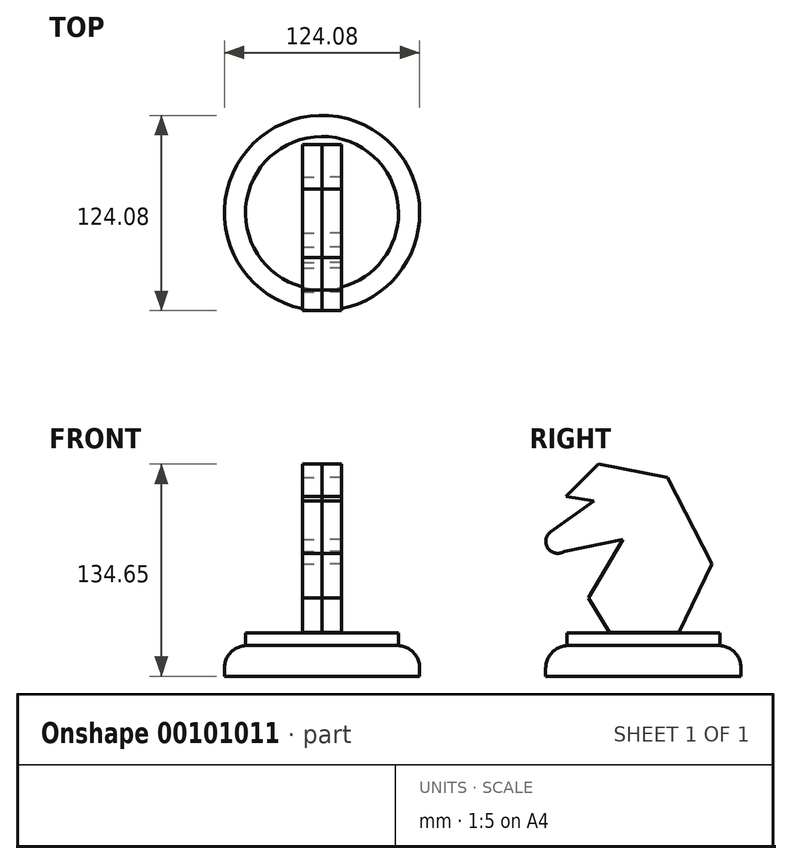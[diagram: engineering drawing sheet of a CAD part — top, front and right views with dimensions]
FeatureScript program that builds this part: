
annotation { "Feature Type Name" : "Feature", "Feature Type Description" : "" }
export const myFeature = defineFeature(function(context is Context, id is Id, definition is map)
    precondition{}
    {
        {
            var Q0;
            Q0=qCreatedBy(makeId("Front.planeOp"),FACE);
            var sketch = newSketch(context, id + "F0", { "sketchPlane" : qUnion([Q0])});
            skLineSegment(sketch, "E0", {"start": v(0, -59.49) * mm, "end": v(-62.04, -59.49) * mm});
            skLineSegment(sketch, "E1", {"start": v(-62.04, -59.49) * mm, "end": v(-62.04, -54.4) * mm});
            skLineSegment(sketch, "E2", {"start": v(0, -32.17) * mm, "end": v(-48.6, -32.17) * mm});
            skLineSegment(sketch, "E3", {"start": v(-48.6, -32.17) * mm, "end": v(-48.6, -40.04) * mm});
            skArc(sketch, "E4", {"start": v(-48.6, -40.04) * mm, "mid": v(-58.16, -44.57) * mm, "end": v(-62.04, -54.4) * mm});
            skLineSegment(sketch, "E5", {"start": v(0, -32.17) * mm, "end": v(0, -59.49) * mm});
            skSolve(sketch);
        }
        {
            var Q0;
            Q0 = qSketchRegion(id + "F0", true);
            var Q1;
            Q1=sQuery(id+"F0.wireOp",EDGE,"E5");
            revolve(context, id + "F1", {"entities" : qUnion([Q0]), "axis" : qUnion([Q1]), "revolveType" : RevolveType.FULL});
        }
        {
            var Q0;
            Q0=qCreatedBy(makeId("Right.planeOp"),FACE);
            var sketch = newSketch(context, id + "F2", { "sketchPlane" : qUnion([Q0])});
            skLineSegment(sketch, "E6", {"start": v(22.71, -31.83) * mm, "end": v(43.63, 11.8) * mm});
            skLineSegment(sketch, "E7", {"start": v(43.63, 11.8) * mm, "end": v(15.24, 66.8) * mm});
            skLineSegment(sketch, "E8", {"start": v(15.24, 66.8) * mm, "end": v(-28.4, 75.16) * mm});
            skLineSegment(sketch, "E9", {"start": v(-28.4, 75.16) * mm, "end": v(-49.01, 54.54) * mm});
            skLineSegment(sketch, "E10", {"start": v(-49.01, 54.54) * mm, "end": v(-31.38, 51.85) * mm});
            skLineSegment(sketch, "E11", {"start": v(-31.38, 51.85) * mm, "end": v(-58.88, 32.13) * mm});
            skArc(sketch, "E12", {"start": v(-58.88, 32.13) * mm, "mid": v(-60.63, 21.7) * mm, "end": v(-50.2, 19.87) * mm});
            skLineSegment(sketch, "E13", {"start": v(-50.2, 19.87) * mm, "end": v(-12.85, 27.35) * mm});
            skLineSegment(sketch, "E14", {"start": v(-12.85, 27.35) * mm, "end": v(-34.97, -9.71) * mm});
            skLineSegment(sketch, "E15", {"start": v(-34.97, -9.71) * mm, "end": v(-21.52, -31.83) * mm});
            skLineSegment(sketch, "E16", {"start": v(-21.52, -31.83) * mm, "end": v(22.71, -31.83) * mm});
            skSolve(sketch);
        }
        {
            var Q0;
            Q0 = qSketchRegion(id + "F2", true);
            extrude(context, id + "F3", {"entities" : qUnion([Q0]), "depth" : 12.5 * mm});
        }
        {
            var Q0;
            Q0=makeQuery(id+"F3.opExtrude","SWEPT_BODY",BODY,{"disambiguationData":[OSD([sQuery(id+"F2.wireOp",EDGE,"E6"),sQuery(id+"F2.wireOp",EDGE,"E7"),sQuery(id+"F2.wireOp",EDGE,"E8"),sQuery(id+"F2.wireOp",EDGE,"E9"),sQuery(id+"F2.wireOp",EDGE,"E10"),sQuery(id+"F2.wireOp",EDGE,"E11"),sQuery(id+"F2.wireOp",EDGE,"E12"),sQuery(id+"F2.wireOp",EDGE,"E13"),sQuery(id+"F2.wireOp",EDGE,"E14"),sQuery(id+"F2.wireOp",EDGE,"E15"),sQuery(id+"F2.wireOp",EDGE,"E16")])]});
            var Q1;
            Q1=makeQuery(id+"F3.opExtrude","CAP_FACE",FACE,{"disambiguationData":[OSD([sQuery(id+"F2.wireOp",EDGE,"E6"),sQuery(id+"F2.wireOp",EDGE,"E7"),sQuery(id+"F2.wireOp",EDGE,"E8"),sQuery(id+"F2.wireOp",EDGE,"E9"),sQuery(id+"F2.wireOp",EDGE,"E10"),sQuery(id+"F2.wireOp",EDGE,"E11"),sQuery(id+"F2.wireOp",EDGE,"E12"),sQuery(id+"F2.wireOp",EDGE,"E13"),sQuery(id+"F2.wireOp",EDGE,"E14"),sQuery(id+"F2.wireOp",EDGE,"E15"),sQuery(id+"F2.wireOp",EDGE,"E16")])],"isStart":true});
            mirror(context, id + "F4", {"operationType" : NewBodyOperationType.ADD, "entities" : qUnion([Q0]), "mirrorPlane" : qUnion([Q1])});
        }
    });
